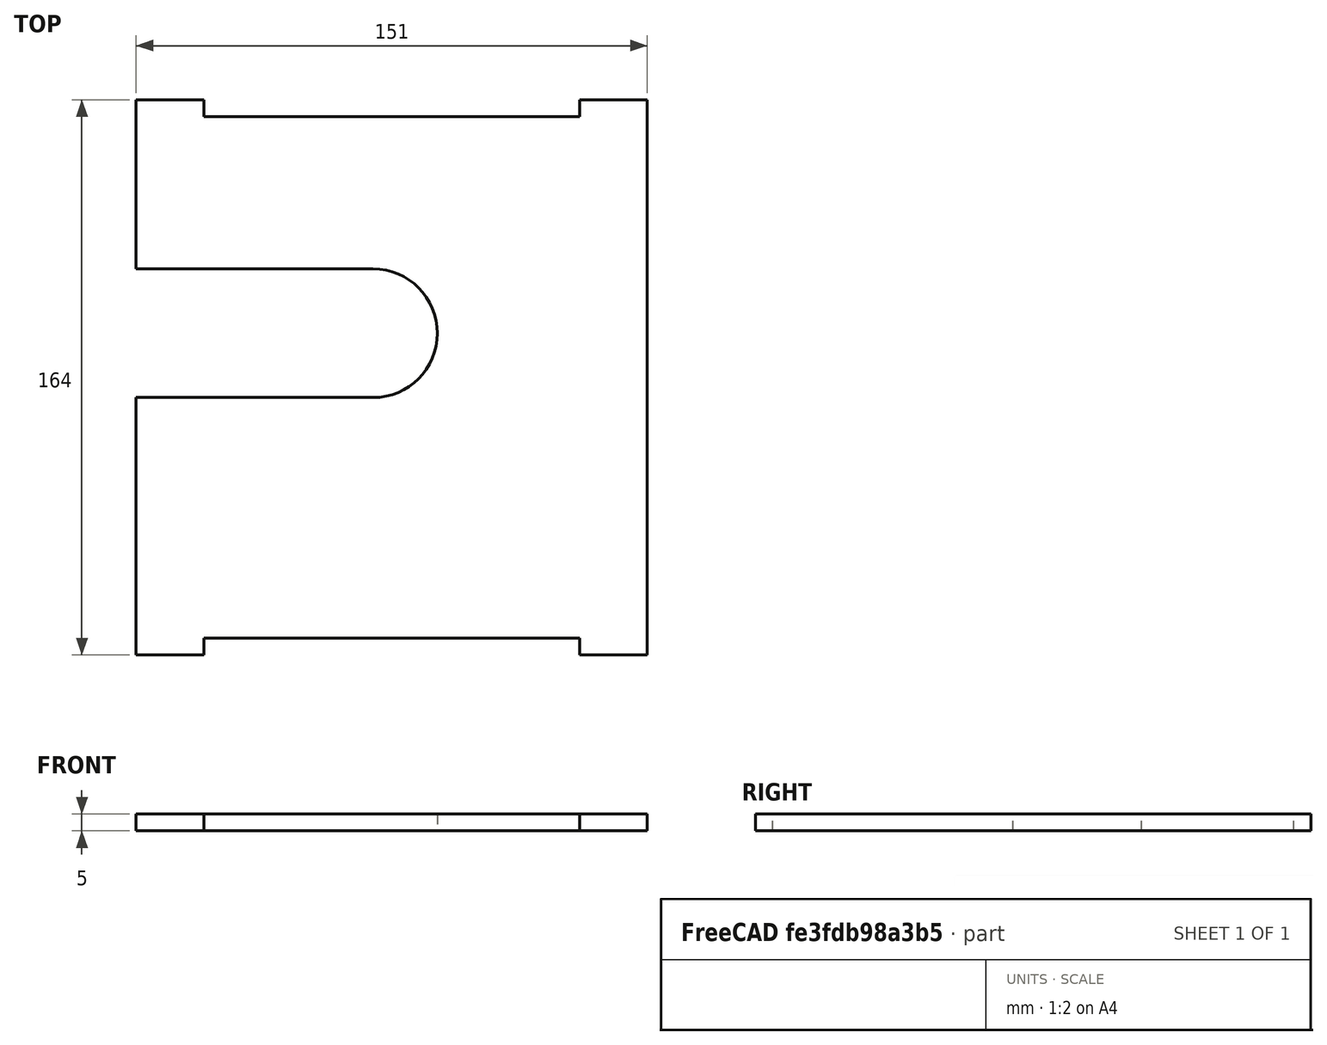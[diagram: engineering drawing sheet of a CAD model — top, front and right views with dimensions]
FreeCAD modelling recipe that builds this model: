
FCSTD DOCUMENT  (FreeCAD 0.15R4671 (Git))
Label: upper_side_axis_B
License: All rights reserved
LicenseURL: http://en.wikipedia.org/wiki/All_rights_reserved
objects: Sketcher::SketchObject×1, PartDesign::Pad×1
note: 3 computed .brp shape members not serialized (recipe doc carries the construction recipe); baked Part::Feature solids carry a one-line shape summary decoded from their .brp

FEATURE [Sketcher::SketchObject] Sketch
  sketch-geometry (16):
    g0: LineSegment StartX=75.5 StartY=82 StartZ=0 EndX=75.5 EndY=-82 EndZ=0
    g1: LineSegment StartX=75.5 StartY=-82 StartZ=0 EndX=55.5 EndY=-82 EndZ=0
    g2: LineSegment StartX=55.5 StartY=-82 StartZ=0 EndX=55.5 EndY=-77 EndZ=0
    g3: LineSegment StartX=55.5 StartY=-77 StartZ=0 EndX=-55.5 EndY=-77 EndZ=0
    g4: LineSegment StartX=-55.5 StartY=-77 StartZ=0 EndX=-55.5 EndY=-82 EndZ=0
    g5: LineSegment StartX=-55.5 StartY=-82 StartZ=0 EndX=-75.5 EndY=-82 EndZ=0
    g6: LineSegment StartX=-75.5 StartY=-82 StartZ=0 EndX=-75.5 EndY=-6 EndZ=0
    g7: LineSegment StartX=-75.5 StartY=32 StartZ=0 EndX=-75.5 EndY=82 EndZ=0
    g8: LineSegment StartX=-75.5 StartY=82 StartZ=0 EndX=-55.5 EndY=82 EndZ=0
    g9: LineSegment StartX=-55.5 StartY=82 StartZ=0 EndX=-55.5 EndY=77 EndZ=0
    g10: LineSegment StartX=-55.5 StartY=77 StartZ=0 EndX=55.5 EndY=77 EndZ=0
    g11: LineSegment StartX=55.5 StartY=77 StartZ=0 EndX=55.5 EndY=82 EndZ=0
    g12: LineSegment StartX=55.5 StartY=82 StartZ=0 EndX=75.5 EndY=82 EndZ=0
    g13: LineSegment StartX=-75.5 StartY=32 StartZ=0 EndX=-5.5 EndY=32 EndZ=0
    g14: ArcOfCircle CenterX=-5.5 CenterY=13 CenterZ=0 NormalX=0 NormalY=0 NormalZ=1 Radius=19 StartAngle=4.71239 EndAngle=7.85398
    g15: LineSegment StartX=-5.5 StartY=-6 StartZ=0 EndX=-75.5 EndY=-6 EndZ=0
  constraints (47):
    c: Coincident(g7,g8)
    c: Coincident(g8,g9)
    c: Coincident(g9,g10)
    c: Coincident(g10,g11)
    c: Coincident(g11,g12)
    c: Coincident(g0,g12)
    c: Coincident(g0,g1)
    c: Coincident(g1,g2)
    c: Coincident(g2,g3)
    c: Coincident(g3,g4)
    c: Coincident(g4,g5)
    c: Coincident(g5,g6)
    c: Horizontal(g5)
    c: Horizontal(g3)
    c: Horizontal(g1)
    c: Horizontal(g12)
    c: Horizontal(g10)
    c: Horizontal(g8)
    c: Vertical(g7)
    c: Vertical(g0)
    c: Vertical(g6)
    c: Vertical(g4)
    c: Vertical(g2)
    c: Vertical(g11)
    c: Vertical(g9)
    c: Equal(g9,g11)
    c: Equal(g11,g2)
    c: Equal(g2,g4)
    c: DistanceY(g4) = -5
    c: DistanceY(g2,g10) = 154
    c: Tangent(g6,g7)
    c: DistanceX(g5,g0) = 151
    c: Equal(g8,g12)
    c: Equal(g12,g1)
    c: Equal(g1,g5)
    c: DistanceX(g3) = -111
    c: Coincident(g7,g13)
    c: Horizontal(g13)
    c: Tangent(g13,g14) = 1.5708
    c: Tangent(g14,g15) = 1.5708
    c: Horizontal(g15)
    c: DistanceY(g14,g10) = 64
    c: Coincident(g15,g6)
    c: Radius(g14) = 19
    c: DistanceX(g7,g14) = 70
    c: Symmetric(g0,g7,g-2)
    c: Symmetric(g0,g0,g-1)
FEATURE [PartDesign::Pad] Pad
  Length = 5
  Length2 = 100
  Midplane = true
  Sketch = -> Sketch
  Type = 0
